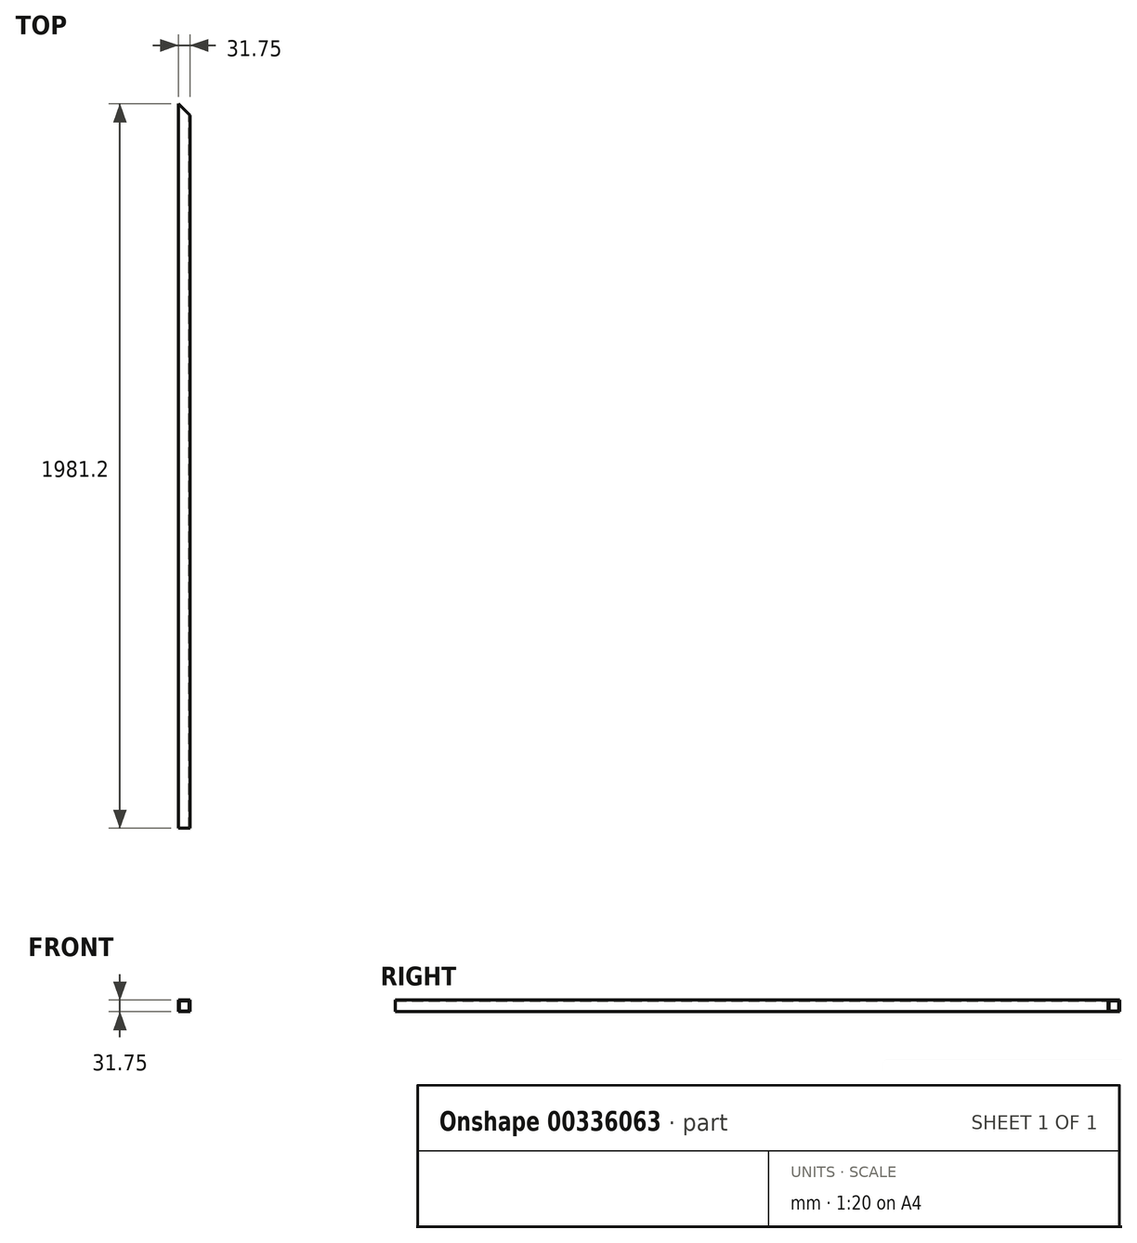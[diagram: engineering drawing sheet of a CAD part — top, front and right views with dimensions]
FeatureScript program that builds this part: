
annotation { "Feature Type Name" : "Feature", "Feature Type Description" : "" }
export const myFeature = defineFeature(function(context is Context, id is Id, definition is map)
    precondition{}
    {
        {
            var Q0;
            Q0=qCreatedBy(makeId("Front.planeOp"),FACE);
            var sketch = newSketch(context, id + "F0", { "sketchPlane" : qUnion([Q0])});
            skLineSegment(sketch, "E0.bottom", {"start": v(-64.17, 32) * mm, "end": v(-32.42, 32) * mm});
            skLineSegment(sketch, "E0.top", {"start": v(-64.17, 0.25) * mm, "end": v(-32.42, 0.25) * mm});
            skLineSegment(sketch, "E0.left", {"start": v(-64.17, 32) * mm, "end": v(-64.17, 0.25) * mm});
            skLineSegment(sketch, "E0.right", {"start": v(-32.42, 32) * mm, "end": v(-32.42, 0.25) * mm});
            skLineSegment(sketch, "E1.0", {"start": v(-34.53, 29.89) * mm, "end": v(-34.53, 2.35) * mm});
            skLineSegment(sketch, "E1.1", {"start": v(-62.06, 29.89) * mm, "end": v(-34.53, 29.89) * mm});
            skLineSegment(sketch, "E1.2", {"start": v(-62.06, 29.89) * mm, "end": v(-62.06, 2.35) * mm});
            skLineSegment(sketch, "E1.3", {"start": v(-62.06, 2.35) * mm, "end": v(-34.53, 2.35) * mm});
            skSolve(sketch);
        }
        {
            var Q0;
            Q0=qSketchRegion(id+"F0",true);
            extrude(context, id + "F1", {"entities" : qUnion([Q0]), "depth" : 1981.2 * mm});
        }
        {
            var Q0;
            Q0=makeQuery(id+"F1.opExtrude","SWEPT_FACE",FACE,{"disambiguationData":[OSD([sQuery(id+"F0.wireOp",EDGE,"E0.bottom")])]});
            var sketch = newSketch(context, id + "F2", { "sketchPlane" : qUnion([Q0])});
            skLineSegment(sketch, "E2", {"start": v(-64.17, 0) * mm, "end": v(-32.42, -31.75) * mm});
            skSolve(sketch);
        }
        {
            var Q0;
            Q0 = qSketchRegion(id + "F2", true);
            var Q1;
            {var subQ0=sQuery(id+"F2.wireOp",EDGE,"E2");Q1=makeQuery(id+"F2.imprint","IMPRINT",FACE,{"disambiguationData":[TD([[makeQuery(id+"F2.imprint","IMPRINT",EDGE,{"derivedFrom":subQ0}),1.0]])]});}
            extrude(context, id + "F3", {"entities" : qUnion([Q0, Q1]), "operationType" : NewBodyOperationType.REMOVE, "oppositeDirection" : true, "depth" : 76.2 * mm});
        }
    });
